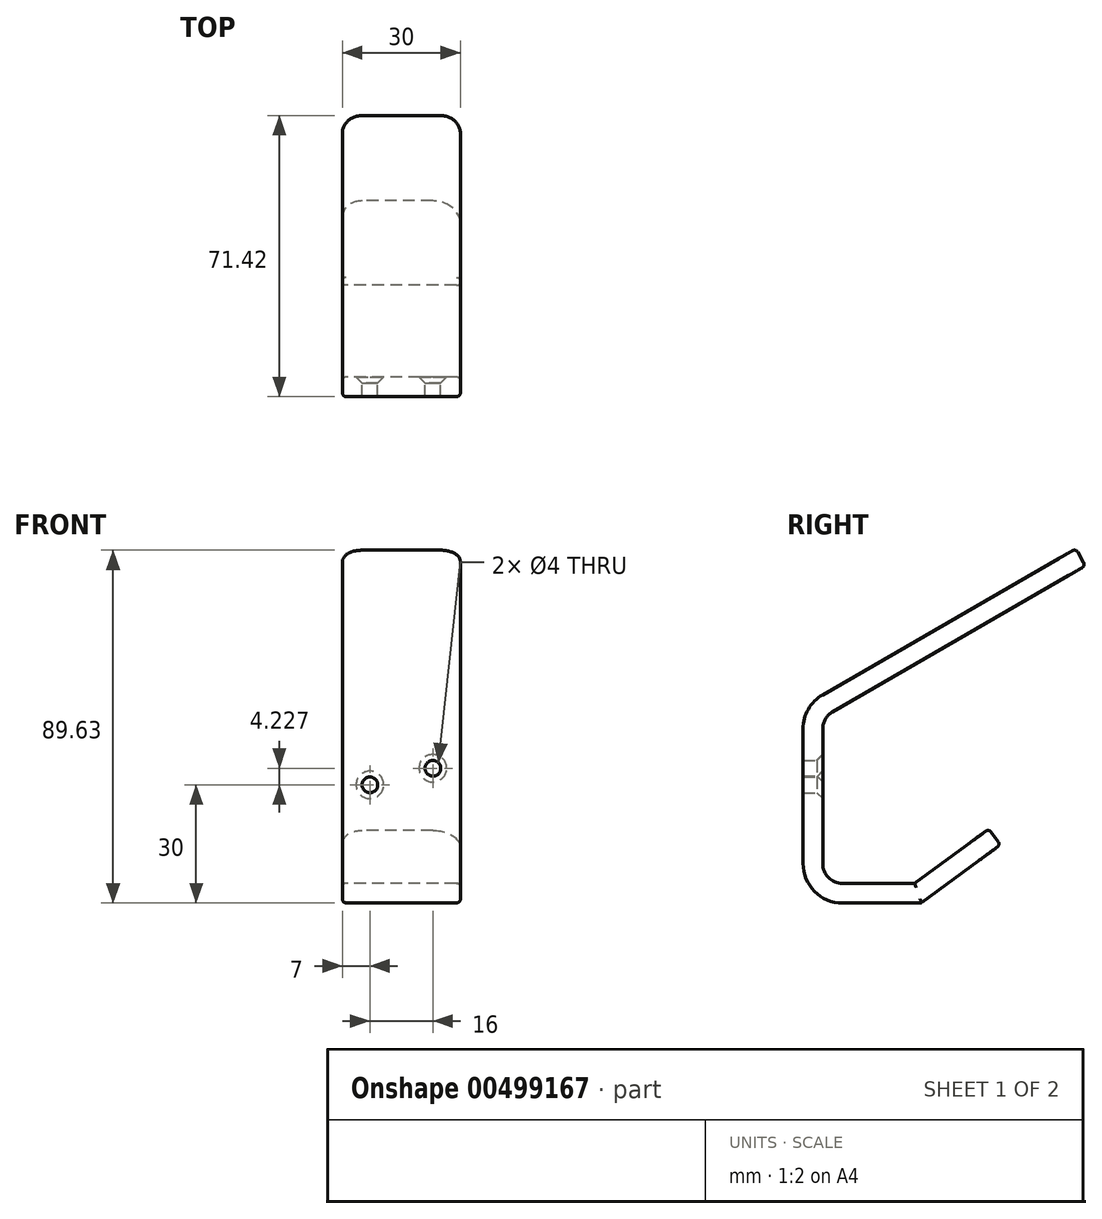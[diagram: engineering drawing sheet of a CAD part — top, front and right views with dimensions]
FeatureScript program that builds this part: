
annotation { "Feature Type Name" : "Feature", "Feature Type Description" : "" }
export const myFeature = defineFeature(function(context is Context, id is Id, definition is map)
    precondition{}
    {
        {
            var Q0;
            Q0=qCreatedBy(makeId("Right.planeOp"),FACE);
            var sketch = newSketch(context, id + "F0", { "sketchPlane" : qUnion([Q0])});
            skLineSegment(sketch, "E0", {"start": v(0, 0) * mm, "end": v(-30, 0) * mm});
            skLineSegment(sketch, "E1", {"start": v(-30, 0) * mm, "end": v(-30, 50) * mm});
            skLineSegment(sketch, "E2", {"start": v(-30, 50) * mm, "end": v(39.28, 90) * mm});
            skLineSegment(sketch, "E3", {"start": v(0, 0) * mm, "end": v(20.16, 14.79) * mm});
            skLineSegment(sketch, "E4", {"start": v(20.16, 14.79) * mm, "end": v(17.2, 18.82) * mm});
            skLineSegment(sketch, "E5", {"start": v(17.2, 18.82) * mm, "end": v(-1.64, 5) * mm});
            skLineSegment(sketch, "E6", {"start": v(39.28, 90) * mm, "end": v(41.78, 85.67) * mm});
            skLineSegment(sketch, "E7", {"start": v(41.78, 85.67) * mm, "end": v(-25, 47.11) * mm});
            skLineSegment(sketch, "E8", {"start": v(-25, 5) * mm, "end": v(-25, 47.11) * mm});
            skLineSegment(sketch, "E9", {"start": v(-25, 5) * mm, "end": v(-1.64, 5) * mm});
            skSolve(sketch);
        }
        {
            var Q0;
            Q0=makeQuery(id+"F0.imprint","IMPRINT",FACE,{"disambiguationData":[TD([[makeQuery(id+"F0.imprint","IMPRINT",EDGE,{"derivedFrom":sQuery(id+"F0.wireOp",EDGE,"E0")}),-1.0]])]});
            extrude(context, id + "F1", {"entities" : qUnion([Q0]), "depth" : 30 * mm});
        }
        {
            var Q0;
            Q0=makeQuery(id+"F1.opExtrude","SWEPT_EDGE",EDGE,{"disambiguationData":[OSD([sQuery(id+"F0.wireOp",EDGE,"E8"),sQuery(id+"F0.wireOp",EDGE,"E9")])]});
            fillet(context, id + "F2", {"entities" : qUnion([Q0]), "radius" : 5 * mm, "tangentPropagation" : true, "allowEdgeOverflow" : false});
        }
        {
            var Q0;
            Q0=makeQuery(id+"F1.opExtrude","CAP_EDGE",EDGE,{"disambiguationData":[OSD([sQuery(id+"F0.wireOp",EDGE,"E4")])],"isStart":false});
            fillet(context, id + "F3", {"entities" : qUnion([Q0]), "radius" : 7 * mm, "tangentPropagation" : true, "allowEdgeOverflow" : false});
        }
        {
            var Q0;
            Q0=makeQuery(id+"F1.opExtrude","CAP_EDGE",EDGE,{"disambiguationData":[OSD([sQuery(id+"F0.wireOp",EDGE,"E4")])],"isStart":true});
            fillet(context, id + "F4", {"entities" : qUnion([Q0]), "radius" : 5 * mm, "tangentPropagation" : true, "allowEdgeOverflow" : false});
        }
        {
            var Q0;
            Q0=makeQuery(id+"F1.opExtrude","CAP_EDGE",EDGE,{"disambiguationData":[OSD([sQuery(id+"F0.wireOp",EDGE,"E6")])],"isStart":true});
            fillet(context, id + "F5", {"entities" : qUnion([Q0]), "radius" : 5 * mm, "tangentPropagation" : true, "allowEdgeOverflow" : false});
        }
        {
            var Q0;
            Q0=makeQuery(id+"F1.opExtrude","CAP_EDGE",EDGE,{"disambiguationData":[OSD([sQuery(id+"F0.wireOp",EDGE,"E6")])],"isStart":false});
            fillet(context, id + "F6", {"entities" : qUnion([Q0]), "radius" : 5 * mm, "tangentPropagation" : true, "allowEdgeOverflow" : false});
        }
        {
            var Q0;
            Q0=makeQuery(id+"F1.opExtrude","CAP_EDGE",EDGE,{"disambiguationData":[OSD([sQuery(id+"F0.wireOp",EDGE,"E9")])],"isStart":true});
            fillet(context, id + "F7", {"entities" : qUnion([Q0]), "radius" : 1 * mm, "tangentPropagation" : true, "allowEdgeOverflow" : false});
        }
        {
            var Q0;
            Q0=makeQuery(id+"F1.opExtrude","CAP_EDGE",EDGE,{"disambiguationData":[OSD([sQuery(id+"F0.wireOp",EDGE,"E5")])],"isStart":true});
            fillet(context, id + "F8", {"entities" : qUnion([Q0]), "radius" : 1 * mm, "tangentPropagation" : true, "allowEdgeOverflow" : false});
        }
        {
            var Q0;
            Q0=makeQuery(id+"F1.opExtrude","CAP_EDGE",EDGE,{"disambiguationData":[OSD([sQuery(id+"F0.wireOp",EDGE,"E3")])],"isStart":false});
            fillet(context, id + "F9", {"entities" : qUnion([Q0]), "radius" : 1 * mm, "tangentPropagation" : true, "allowEdgeOverflow" : false});
        }
        {
            var Q0;
            Q0=makeQuery(id+"F1.opExtrude","SWEPT_EDGE",EDGE,{"disambiguationData":[OSD([sQuery(id+"F0.wireOp",EDGE,"E7"),sQuery(id+"F0.wireOp",EDGE,"E8")])]});
            fillet(context, id + "F10", {"entities" : qUnion([Q0]), "radius" : 5 * mm, "tangentPropagation" : true, "allowEdgeOverflow" : false});
        }
        {
            var Q0;
            Q0=makeQuery(id+"F1.opExtrude","SWEPT_FACE",FACE,{"disambiguationData":[OSD([sQuery(id+"F0.wireOp",EDGE,"E8")])]});
            var sketch = newSketch(context, id + "F11", { "sketchPlane" : qUnion([Q0])});
            skPoint(sketch, "E10", {"position": v(-23, 34.23) * mm});
            skPoint(sketch, "E11", {"position": v(-7, 30) * mm});
            skSolve(sketch);
        }
        {
            var Q0;
            Q0=sQuery(id+"F11.wireOp",VERTEX,"E10");
            var Q1;
            Q1=sQuery(id+"F11.wireOp",VERTEX,"E11");
            var Q2;
            Q2=makeQuery(id+"F1.opExtrude","SWEPT_BODY",BODY,{"disambiguationData":[OSD([sQuery(id+"F0.wireOp",EDGE,"E0"),sQuery(id+"F0.wireOp",EDGE,"E1"),sQuery(id+"F0.wireOp",EDGE,"E2"),sQuery(id+"F0.wireOp",EDGE,"E3"),sQuery(id+"F0.wireOp",EDGE,"E4"),sQuery(id+"F0.wireOp",EDGE,"E5"),sQuery(id+"F0.wireOp",EDGE,"E6"),sQuery(id+"F0.wireOp",EDGE,"E7"),sQuery(id+"F0.wireOp",EDGE,"E8"),sQuery(id+"F0.wireOp",EDGE,"E9")])]});
            hole(context, id + "F12", {"style" : HoleStyle.C_SINK, "endStyle" : HoleEndStyle.THROUGH, "holeDiameter" : 4 * mm, "cSinkDiameter" : 7 * mm, "cSinkAngle" : 90 * degree, "isTappedThrough" : true, "tappedDepth" : 12 * mm, "tapClearance" : 3, "locations" : qUnion([Q0, Q1]), "scope" : qUnion([Q2])});
        }
        {
            var Q0;
            Q0=makeQuery(id+"F1.opExtrude","SWEPT_EDGE",EDGE,{"disambiguationData":[OSD([sQuery(id+"F0.wireOp",EDGE,"E0"),sQuery(id+"F0.wireOp",EDGE,"E1")])]});
            fillet(context, id + "F13", {"entities" : qUnion([Q0]), "radius" : 10 * mm, "tangentPropagation" : true, "allowEdgeOverflow" : false});
        }
        {
            var Q0;
            Q0=makeQuery(id+"F1.opExtrude","SWEPT_EDGE",EDGE,{"disambiguationData":[OSD([sQuery(id+"F0.wireOp",EDGE,"E1"),sQuery(id+"F0.wireOp",EDGE,"E2")])]});
            fillet(context, id + "F14", {"entities" : qUnion([Q0]), "radius" : 10 * mm, "tangentPropagation" : true, "allowEdgeOverflow" : false});
        }
        {
            var Q0;
            Q0=makeQuery(id+"F1.opExtrude","CAP_EDGE",EDGE,{"disambiguationData":[OSD([sQuery(id+"F0.wireOp",EDGE,"E1")])],"isStart":false});
            var Q1;
            {var subQ0=sQuery(id+"F0.wireOp",EDGE,"E2");var subQ1=sQuery(id+"F0.wireOp",EDGE,"E1");Q1=makeQuery(id+"F14.opFillet","BLEND_EDGE",EDGE,{"blendedFrom":[makeQuery(id+"F1.opExtrude","SWEPT_EDGE",EDGE,{"disambiguationData":[OSD([subQ1,subQ0])]}),makeQuery(id+"F1.opExtrude","CAP_FACE",FACE,{"disambiguationData":[OSD([sQuery(id+"F0.wireOp",EDGE,"E0"),subQ1,subQ0,sQuery(id+"F0.wireOp",EDGE,"E3"),sQuery(id+"F0.wireOp",EDGE,"E4"),sQuery(id+"F0.wireOp",EDGE,"E5"),sQuery(id+"F0.wireOp",EDGE,"E6"),sQuery(id+"F0.wireOp",EDGE,"E7"),sQuery(id+"F0.wireOp",EDGE,"E8"),sQuery(id+"F0.wireOp",EDGE,"E9")])],"isStart":false})],"blendedInto":[makeQuery(id+"F1.opExtrude","CAP_FACE",FACE,{"disambiguationData":[OSD([sQuery(id+"F0.wireOp",EDGE,"E0"),subQ1,subQ0,sQuery(id+"F0.wireOp",EDGE,"E3"),sQuery(id+"F0.wireOp",EDGE,"E4"),sQuery(id+"F0.wireOp",EDGE,"E5"),sQuery(id+"F0.wireOp",EDGE,"E6"),sQuery(id+"F0.wireOp",EDGE,"E7"),sQuery(id+"F0.wireOp",EDGE,"E8"),sQuery(id+"F0.wireOp",EDGE,"E9")])],"isStart":false})]});}
            fillet(context, id + "F15", {"entities" : qUnion([Q0, Q1]), "radius" : 1 * mm, "tangentPropagation" : true, "allowEdgeOverflow" : false});
        }
        {
            var Q0;
            Q0=makeQuery(id+"F1.opExtrude","CAP_EDGE",EDGE,{"disambiguationData":[OSD([sQuery(id+"F0.wireOp",EDGE,"E7")])],"isStart":false});
            fillet(context, id + "F16", {"entities" : qUnion([Q0]), "radius" : 1 * mm, "tangentPropagation" : true, "allowEdgeOverflow" : false});
        }
    });
